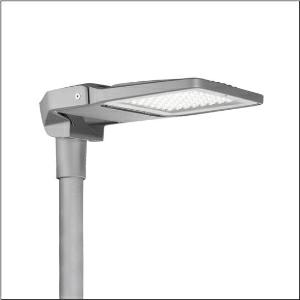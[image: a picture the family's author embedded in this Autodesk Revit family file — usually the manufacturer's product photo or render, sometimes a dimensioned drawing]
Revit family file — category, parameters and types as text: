
# Revit family: floodlight_fl_20_mini___pl52_5xa7672b1d4ac_42ec
name_source: partatom
category: Lighting Fixtures
units: mm (PartAtom-declared; Revit-internal decimal feet)

## family parameters
Cut with Voids When Loaded = No
Host = Face
Light Source = No
Part Type = Normal
Room Calculation Point = No
Round Connector Dimension = Use Diameter
Shared = No

## types (1)
- --- (1 x LED 3000K / CRI = 80 (unbekannt), 4930 lm, 3000K)
    Apparent Load = 51 VA
    CIE Flux Codes = 27 59 98 100 100
    Color Rendering = 80
    Color Temperature = 3000K
    Default Elevation = 1800 mm
    Description = Floodlight FL 20 mini, floodlight, primary light control with lens, of plastic, primary optical cover: protective disc, of toughened safety glass, transparent, light distribution: PL52, light emission: direct distribution, primary light characteristic: asymmetric, installation type: side-entry, post-top, LED, High Power LED, rated luminous flux: 4.930lm, luminous efficacy: 97lm/W, light colour: 830, colour temperature: 3000K, control gear: ECG Plus, control: flexible luminous flux parameterisation, time-dependent luminous flux control, digital communication interface, overheat protection, power reduction, electronic power reduction, with terminal, 5-pole, max. 2.5mm², mains connection: 220..240V, AC, 50/60Hz, rated input power: 51W, LED unit, of diecast aluminium, powder-coated, Siteco® metallic grey (DB 702S), corrosivity category C5 mid according to DIN EN ISO 12944, incl. 1x M20 cable gland for cable Ø 6.5..12mm, inclination adjustable: 0°, 5°, 10°, 15°, please order mast flange separately, length: 565mm, width: 335mm, height: 119mm, housing frame, of diecast aluminium, powder-coated, Siteco® metallic grey (DB 702S), mast flange adapter, of diecast aluminium, powder-coated, Siteco® metallic grey (DB 702S), DALI, protection rating (complete): IP66, insulation class (complete): insulation class II (safety insulation), certification: CE, ENEC, VDE, protection symbol: D, permissible operating ambient temperature: -40..+40°C, permissible operating ambient temperature for outdoor applications: -40..+50°C, standard: DIN EN 12944, packaging unit: 1 piece

Light Distribution: PL52
    Height = 62 mm  [stored 0.203412 ft]
    Lamp = 1 x LED 3000K / CRI >= 80 (unbekannt)
    Lamp Light Flux = 4930 lm
    Lamp count = 1
    Length = 565 mm
    Luminous efficacy = 97 lm/W
    Manufacturer = Siteco
    ModVariant = No
    Model = 5XA7672B1D4AC
    Number of Poles = 1
    OnlyDefault = Yes
    Power Factor = 1
    Product Name = Floodlight FL 20 mini | PL52
    Product group = floodlight | pylon top
    ProductGroupID = 6101
    Protection Class = Protection class II
    Protection Degree = IP 66
    RLX_Detail_Level = 1
    RLX_Emergency_Light_Flux = 0 lm
    RLX_Emergency_Type = 0
    RLX_Emergency_Type_DB = No
    RlxData = <blob elided: 102057 chars, md5=a20a2840>
    Socket = socket
    Standby Power = 0 W
    System Light Flux = 4930 lm
    System Power = 51 W
    Type Comments = factory setting: luminous flux: 100 % | dim-lin: 254 | 520 mA
    Type Image = l_1005946.jpg
    URL = http://relux.com
    VarID = @adj_163705
    Voltage = 0 V
    Weight = 0.00 kg
    Width = 335 mm

note: [stored X ft] marks values corroborated as IEEE doubles in the binary element streams (Revit-internal decimal feet)

## geometry (parser evidence)
native form markers: Blend x4, Sweep x13
no freeform markers — native parametric forms only
